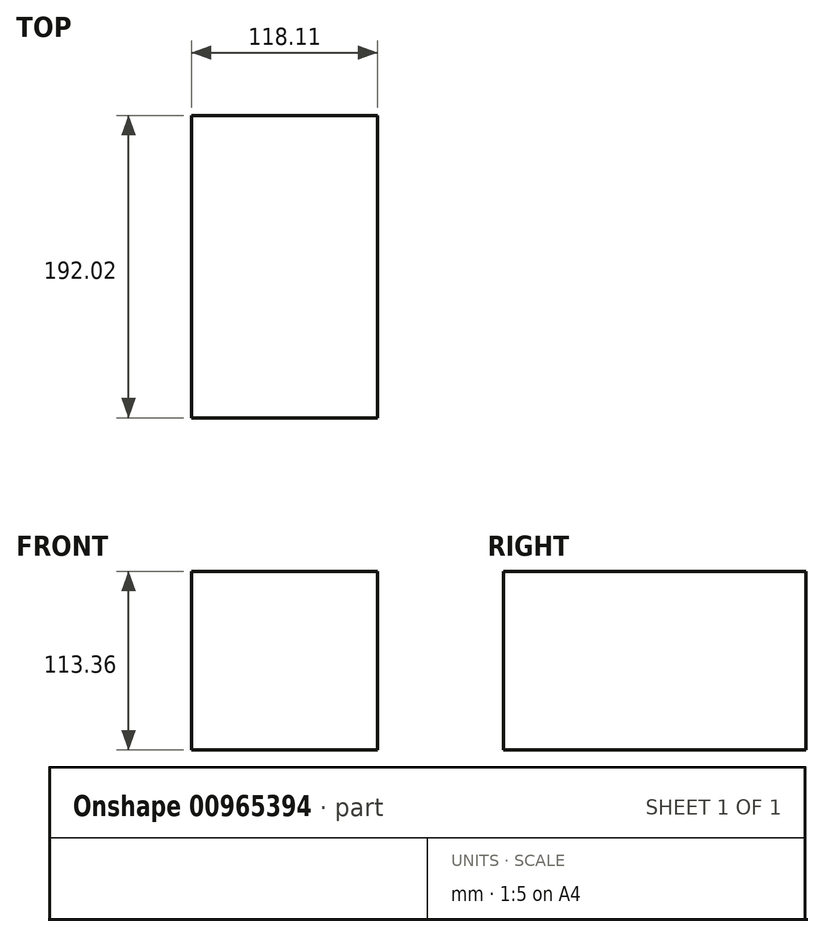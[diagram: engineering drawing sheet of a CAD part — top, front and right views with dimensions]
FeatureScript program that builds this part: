
annotation { "Feature Type Name" : "Feature", "Feature Type Description" : "" }
export const myFeature = defineFeature(function(context is Context, id is Id, definition is map)
    precondition{}
    {
        {
            var Q0;
            Q0=qCreatedBy(makeId("Front.planeOp"),FACE);
            var sketch = newSketch(context, id + "F0", { "sketchPlane" : qUnion([Q0])});
            skLineSegment(sketch, "E0.bottom", {"start": v(0, 0) * mm, "end": v(0, 0) * mm});
            skLineSegment(sketch, "E0.top", {"start": v(0, -13.71) * mm, "end": v(0, -13.71) * mm});
            skLineSegment(sketch, "E0.left", {"start": v(0, 0) * mm, "end": v(0, -13.71) * mm});
            skLineSegment(sketch, "E0.right", {"start": v(0, 0) * mm, "end": v(0, -13.71) * mm});
            skLineSegment(sketch, "E1.bottom", {"start": v(-61.85, -42.6) * mm, "end": v(56.26, -42.6) * mm});
            skLineSegment(sketch, "E1.top", {"start": v(-61.85, 70.76) * mm, "end": v(56.26, 70.76) * mm});
            skLineSegment(sketch, "E1.left", {"start": v(-61.85, -42.6) * mm, "end": v(-61.85, 70.76) * mm});
            skLineSegment(sketch, "E1.right", {"start": v(56.26, -42.6) * mm, "end": v(56.26, 70.76) * mm});
            skSolve(sketch);
        }
        {
            var Q0;
            Q0 = qSketchRegion(id + "F0", true);
            extrude(context, id + "F1", {"entities" : qUnion([Q0]), "depth" : 192.02 * mm, "offsetDistance" : 25.4 * mm});
        }
    });
